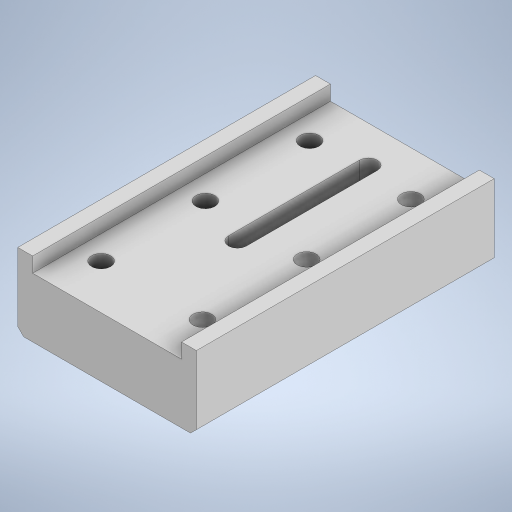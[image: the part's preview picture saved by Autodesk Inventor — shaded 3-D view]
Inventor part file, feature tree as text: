
AUTODESK INVENTOR PART (.ipt)
format: ipt  version: 2023.2 (Build 272271030, 271C)  size: 334,336 bytes
history: native  units: mm
features: sketch x4, extrude x3, chamfer x2, hole x1
ambient origin geometry x8: Origin, YZ Plane, XZ Plane, XY Plane, X Axis, Y Axis, Z Axis, Center Point
bodies: Solid1 (feature_tree)
feature tree (10):
  extrude  "Extrusion1"  Depth=30.0mm
  extrude  "Extrusion2"  Depth=100.0mm
  hole  "Hole1"  [1 undecoded]
  extrude  "Extrusion4"  Depth=2.0mm
  chamfer  "Chamfer1"  Distance=11.0mm
  chamfer  "Chamfer2"  Distance=15.0mm
  sketch  "Sketch1"  dims[d0=30.0mm d1=30.0mm]
  sketch  "Sketch2"  dims[d2=100.0mm d3=11.0mm]
  sketch  "Sketch4"  dims[d4=11.0mm d5=11.0mm]
  sketch  "Sketch5"  dims[d6=11.0mm d7=11.0mm d8=11.0mm d9=15.0mm d10=35.0mm d11=70.0mm d12=13.0mm d13=6.0mm d14=6.0mm d15=44.0mm d16=13.0mm d17=6.0mm d18=0.0mm d19=6.4mm d21=6.4mm d22=6.4mm d23=6.4mm d24=6.4mm d25=15.0mm d26=35.0mm d27=70.0mm d28=13.0mm d29=13.0mm d30=6.4mm d31=6.0mm d36=14.0mm d37=0.0mm d43=8.0mm d44=8.0mm d45=10.0mm d46=20.0mm d47=20.0mm d48=8.0mm d49=6.0mm d50=4.0mm d51=2.0mm d52=90.0deg d53=12.0mm d54=20.594885mm d55=100.0mm d56=5.0mm d57=100.0mm d58=5.0mm d59=5.0mm d60=0.0mm d61=2.0mm d62=2.0mm d63=45.0deg d64=2.0mm d65=2.0mm d66=45.0deg d41=0.5mm d42=0.872665mm]
note: 1 required parameter value undecoded (feature->parameter linkage not recoverable at this tier; creation-order binding heuristic only, values carry confidence <= 0.55)
